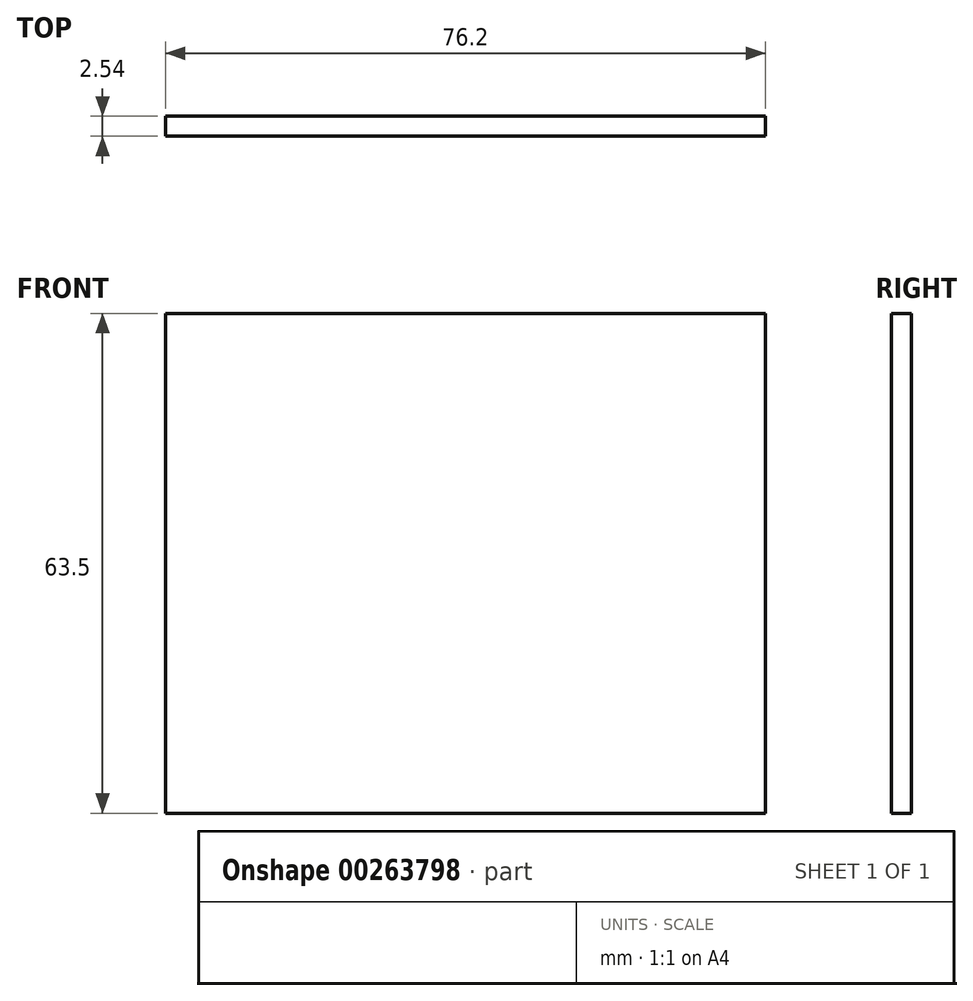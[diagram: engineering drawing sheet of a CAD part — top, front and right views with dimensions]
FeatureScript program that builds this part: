
annotation { "Feature Type Name" : "Feature", "Feature Type Description" : "" }
export const myFeature = defineFeature(function(context is Context, id is Id, definition is map)
    precondition{}
    {
        {
            var Q0;
            Q0=qCreatedBy(makeId("Front.planeOp"),FACE);
            var sketch = newSketch(context, id + "F0", { "sketchPlane" : qUnion([Q0])});
            skLineSegment(sketch, "E0.bottom", {"start": v(10.64, 19.17) * mm, "end": v(-65.56, 19.17) * mm});
            skLineSegment(sketch, "E0.top", {"start": v(10.64, 82.67) * mm, "end": v(-65.56, 82.67) * mm});
            skLineSegment(sketch, "E0.left", {"start": v(10.64, 19.17) * mm, "end": v(10.64, 82.67) * mm});
            skLineSegment(sketch, "E0.right", {"start": v(-65.56, 19.17) * mm, "end": v(-65.56, 82.67) * mm});
            skPoint(sketch, "E0.middle", {"position": v(-27.46, 50.92) * mm});
            skSolve(sketch);
        }
        {
            var Q0;
            Q0 = qSketchRegion(id + "F0", true);
            extrude(context, id + "F1", {"entities" : qUnion([Q0]), "depth" : 2.54 * mm});
        }
    });
